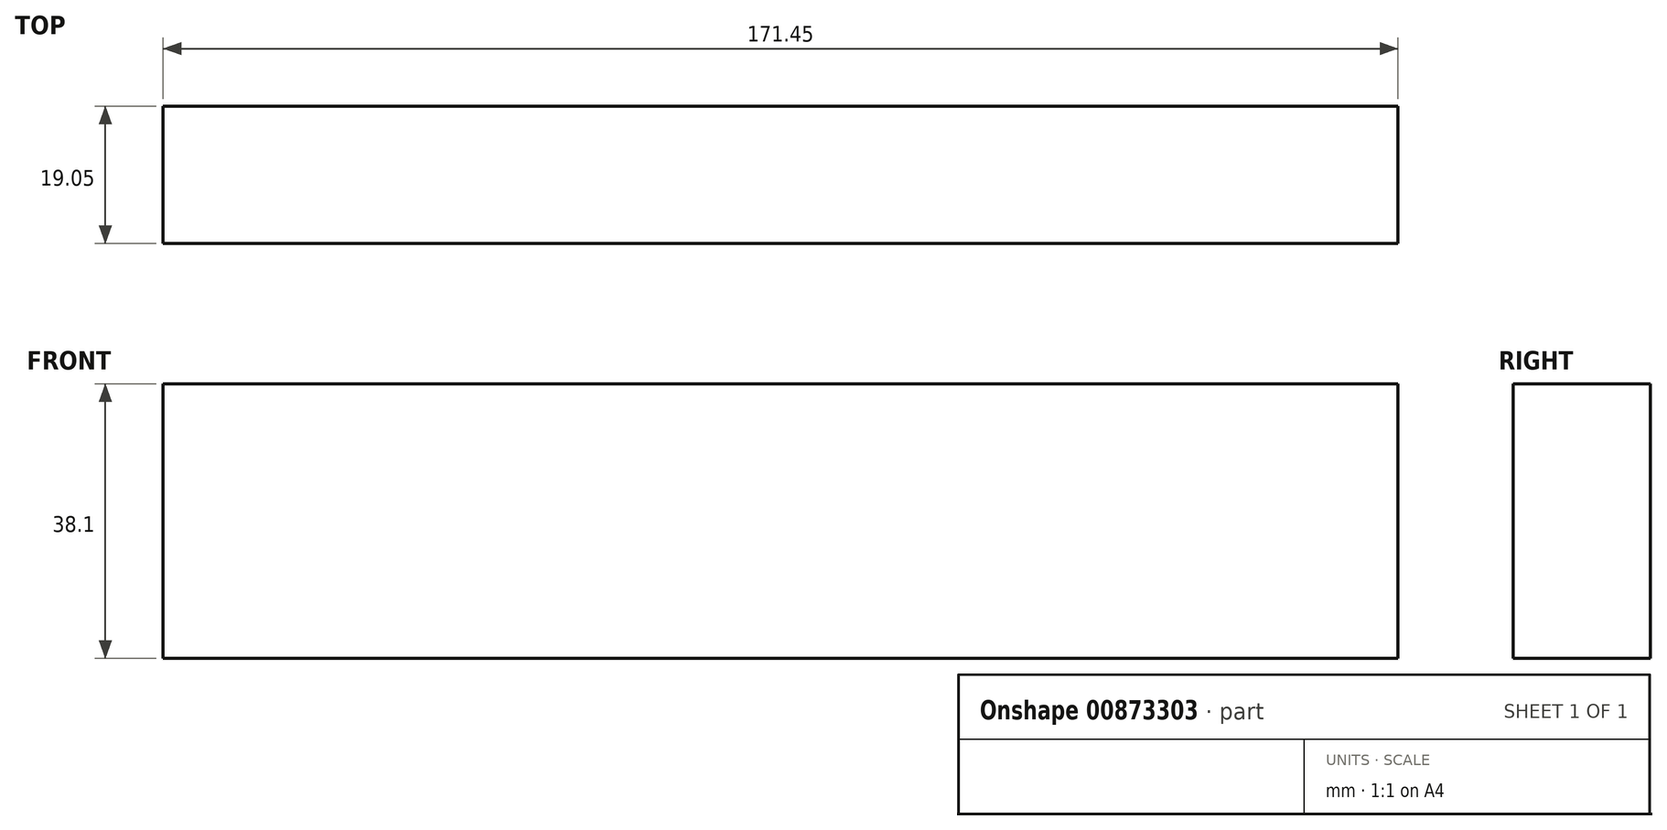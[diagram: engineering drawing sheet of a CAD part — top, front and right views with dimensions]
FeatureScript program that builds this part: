
annotation { "Feature Type Name" : "Feature", "Feature Type Description" : "" }
export const myFeature = defineFeature(function(context is Context, id is Id, definition is map)
    precondition{}
    {
        {
            var Q0;
            Q0=qCreatedBy(makeId("Front.planeOp"),FACE);
            var sketch = newSketch(context, id + "F0", { "sketchPlane" : qUnion([Q0])});
            skLineSegment(sketch, "E0.bottom", {"start": v(0, 0) * mm, "end": v(-171.45, 0) * mm});
            skLineSegment(sketch, "E0.top", {"start": v(0, 38.1) * mm, "end": v(-171.45, 38.1) * mm});
            skLineSegment(sketch, "E0.left", {"start": v(0, 0) * mm, "end": v(0, 38.1) * mm});
            skLineSegment(sketch, "E0.right", {"start": v(-171.45, 0) * mm, "end": v(-171.45, 38.1) * mm});
            skSolve(sketch);
        }
        {
            var Q0;
            Q0 = qSketchRegion(id + "F0", true);
            extrude(context, id + "F1", {"entities" : qUnion([Q0]), "depth" : 19.05 * mm, "offsetDistance" : 25.4 * mm});
        }
    });
